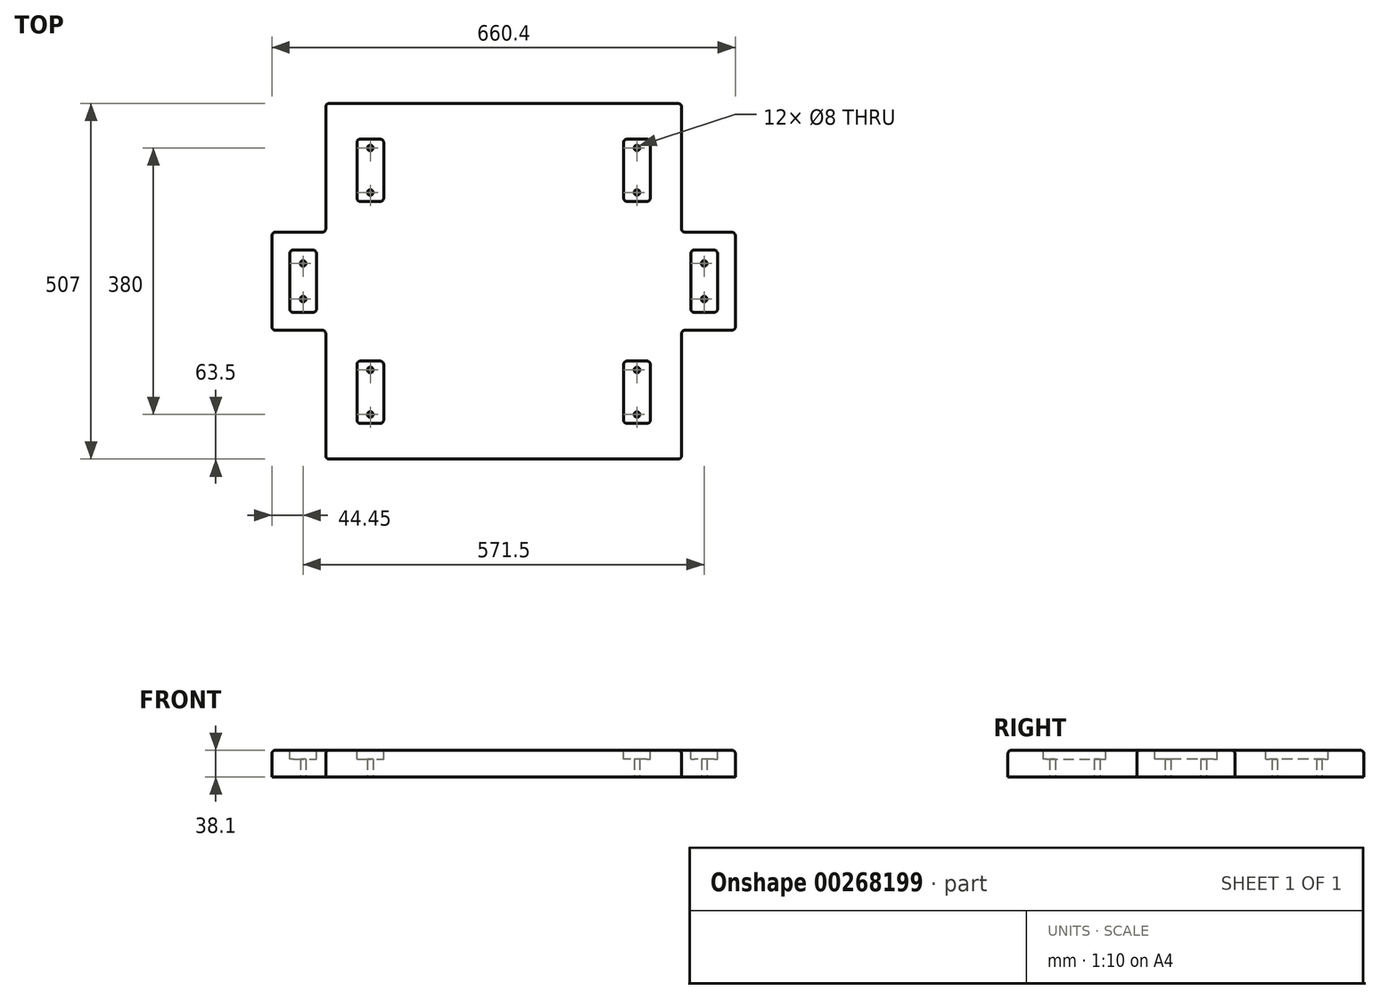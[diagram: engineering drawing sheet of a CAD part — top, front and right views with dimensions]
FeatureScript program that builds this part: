
annotation { "Feature Type Name" : "Feature", "Feature Type Description" : "" }
export const myFeature = defineFeature(function(context is Context, id is Id, definition is map)
    precondition{}
    {
        {
            var Q0;
            Q0=qCreatedBy(makeId("Top.planeOp"),FACE);
            var sketch = newSketch(context, id + "F0", { "sketchPlane" : qUnion([Q0])});
            skLineSegment(sketch, "E0.bottom", {"start": v(-253.5, 253.5) * mm, "end": v(253.5, 253.5) * mm});
            skLineSegment(sketch, "E0.top", {"start": v(-253.5, -253.5) * mm, "end": v(253.5, -253.5) * mm});
            skLineSegment(sketch, "E0.left", {"start": v(-253.5, 253.5) * mm, "end": v(-253.5, 69.85) * mm});
            skLineSegment(sketch, "E0.right", {"start": v(253.5, 253.5) * mm, "end": v(253.5, 69.85) * mm});
            skCircle(sketch, "E1", {"center": v(-190, 190) * mm, "radius": 4 * mm});
            skCircle(sketch, "E2", {"center": v(-190, 126.5) * mm, "radius": 4 * mm});
            skCircle(sketch, "E3.MirrorC", {"center": v(190, 126.5) * mm, "radius": 4 * mm});
            skCircle(sketch, "E4.MirrorC", {"center": v(190, 190) * mm, "radius": 4 * mm});
            skCircle(sketch, "E5.MirrorC", {"center": v(190, -190) * mm, "radius": 4 * mm});
            skCircle(sketch, "E6.MirrorC", {"center": v(190, -126.5) * mm, "radius": 4 * mm});
            skCircle(sketch, "E7.MirrorC", {"center": v(-190, -126.5) * mm, "radius": 4 * mm});
            skCircle(sketch, "E8.MirrorC", {"center": v(-190, -190) * mm, "radius": 4 * mm});
            skLineSegment(sketch, "E9.bottom", {"start": v(330.2, 69.85) * mm, "end": v(253.5, 69.85) * mm});
            skLineSegment(sketch, "E9.top", {"start": v(330.2, -69.85) * mm, "end": v(253.5, -69.85) * mm});
            skLineSegment(sketch, "E9.left", {"start": v(330.2, 69.85) * mm, "end": v(330.2, -69.85) * mm});
            skLineSegment(sketch, "E9.right", {"start": v(-330.2, 69.85) * mm, "end": v(-330.2, -69.85) * mm});
            skLineSegment(sketch, "E10.trimOffspring", {"start": v(-253.5, 69.85) * mm, "end": v(-330.2, 69.85) * mm});
            skLineSegment(sketch, "E11.trimOffspring", {"start": v(-253.5, -69.85) * mm, "end": v(-253.5, -253.5) * mm});
            skLineSegment(sketch, "E12.trimOffspring", {"start": v(-253.5, -69.85) * mm, "end": v(-330.2, -69.85) * mm});
            skLineSegment(sketch, "E13.trimOffspring", {"start": v(253.5, -69.85) * mm, "end": v(253.5, -253.5) * mm});
            skCircle(sketch, "E14", {"center": v(-285.75, 25.4) * mm, "radius": 4 * mm});
            skCircle(sketch, "E15.MirrorC", {"center": v(-285.75, -25.4) * mm, "radius": 4 * mm});
            skCircle(sketch, "E16.MirrorC", {"center": v(285.75, -25.4) * mm, "radius": 4 * mm});
            skCircle(sketch, "E17.MirrorC", {"center": v(285.75, 25.4) * mm, "radius": 4 * mm});
            skSolve(sketch);
        }
        {
            var Q0;
            Q0=makeQuery(id+"F0.imprint","IMPRINT",FACE,{"disambiguationData":[TD([[makeQuery(id+"F0.imprint","IMPRINT",EDGE,{"derivedFrom":sQuery(id+"F0.wireOp",EDGE,"E0.bottom")}),-1.0]])]});
            extrude(context, id + "F1", {"entities" : qUnion([Q0]), "depth" : 38.1 * mm});
        }
        {
            var Q0;
            Q0=makeQuery(id+"F1.opExtrude","CAP_EDGE",EDGE,{"disambiguationData":[OSD([sQuery(id+"F0.wireOp",EDGE,"E0.top")])],"isStart":false});
            var Q1;
            Q1=makeQuery(id+"F1.opExtrude","CAP_EDGE",EDGE,{"disambiguationData":[OSD([sQuery(id+"F0.wireOp",EDGE,"E11.trimOffspring")])],"isStart":false});
            var Q2;
            Q2=makeQuery(id+"F1.opExtrude","SWEPT_EDGE",EDGE,{"disambiguationData":[OSD([sQuery(id+"F0.wireOp",EDGE,"E0.top"),sQuery(id+"F0.wireOp",EDGE,"E11.trimOffspring")])]});
            var Q3;
            Q3=makeQuery(id+"F1.opExtrude","SWEPT_EDGE",EDGE,{"disambiguationData":[OSD([sQuery(id+"F0.wireOp",EDGE,"E11.trimOffspring"),sQuery(id+"F0.wireOp",EDGE,"E12.trimOffspring")])]});
            var Q4;
            Q4=makeQuery(id+"F1.opExtrude","CAP_EDGE",EDGE,{"disambiguationData":[OSD([sQuery(id+"F0.wireOp",EDGE,"E12.trimOffspring")])],"isStart":false});
            var Q5;
            Q5=makeQuery(id+"F1.opExtrude","SWEPT_EDGE",EDGE,{"disambiguationData":[OSD([sQuery(id+"F0.wireOp",EDGE,"E9.right"),sQuery(id+"F0.wireOp",EDGE,"E12.trimOffspring")])]});
            var Q6;
            Q6=makeQuery(id+"F1.opExtrude","CAP_EDGE",EDGE,{"disambiguationData":[OSD([sQuery(id+"F0.wireOp",EDGE,"E9.right")])],"isStart":false});
            var Q7;
            Q7=makeQuery(id+"F1.opExtrude","CAP_EDGE",EDGE,{"disambiguationData":[OSD([sQuery(id+"F0.wireOp",EDGE,"E10.trimOffspring")])],"isStart":false});
            var Q8;
            Q8=makeQuery(id+"F1.opExtrude","CAP_EDGE",EDGE,{"disambiguationData":[OSD([sQuery(id+"F0.wireOp",EDGE,"E0.left")])],"isStart":false});
            var Q9;
            Q9=makeQuery(id+"F1.opExtrude","CAP_EDGE",EDGE,{"disambiguationData":[OSD([sQuery(id+"F0.wireOp",EDGE,"E0.bottom")])],"isStart":false});
            var Q10;
            Q10=makeQuery(id+"F1.opExtrude","CAP_EDGE",EDGE,{"disambiguationData":[OSD([sQuery(id+"F0.wireOp",EDGE,"E0.right")])],"isStart":false});
            var Q11;
            Q11=makeQuery(id+"F1.opExtrude","CAP_EDGE",EDGE,{"disambiguationData":[OSD([sQuery(id+"F0.wireOp",EDGE,"E9.bottom")])],"isStart":false});
            var Q12;
            Q12=makeQuery(id+"F1.opExtrude","SWEPT_EDGE",EDGE,{"disambiguationData":[OSD([sQuery(id+"F0.wireOp",EDGE,"E0.right"),sQuery(id+"F0.wireOp",EDGE,"E9.bottom")])]});
            var Q13;
            Q13=makeQuery(id+"F1.opExtrude","SWEPT_EDGE",EDGE,{"disambiguationData":[OSD([sQuery(id+"F0.wireOp",EDGE,"E0.bottom"),sQuery(id+"F0.wireOp",EDGE,"E0.right")])]});
            var Q14;
            Q14=makeQuery(id+"F1.opExtrude","SWEPT_EDGE",EDGE,{"disambiguationData":[OSD([sQuery(id+"F0.wireOp",EDGE,"E0.bottom"),sQuery(id+"F0.wireOp",EDGE,"E0.left")])]});
            var Q15;
            Q15=makeQuery(id+"F1.opExtrude","SWEPT_EDGE",EDGE,{"disambiguationData":[OSD([sQuery(id+"F0.wireOp",EDGE,"E0.left"),sQuery(id+"F0.wireOp",EDGE,"E10.trimOffspring")])]});
            var Q16;
            Q16=makeQuery(id+"F1.opExtrude","SWEPT_EDGE",EDGE,{"disambiguationData":[OSD([sQuery(id+"F0.wireOp",EDGE,"E9.right"),sQuery(id+"F0.wireOp",EDGE,"E10.trimOffspring")])]});
            var Q17;
            Q17=makeQuery(id+"F1.opExtrude","CAP_EDGE",EDGE,{"disambiguationData":[OSD([sQuery(id+"F0.wireOp",EDGE,"E9.top")])],"isStart":false});
            var Q18;
            Q18=makeQuery(id+"F1.opExtrude","CAP_EDGE",EDGE,{"disambiguationData":[OSD([sQuery(id+"F0.wireOp",EDGE,"E9.left")])],"isStart":false});
            var Q19;
            Q19=makeQuery(id+"F1.opExtrude","SWEPT_EDGE",EDGE,{"disambiguationData":[OSD([sQuery(id+"F0.wireOp",EDGE,"E9.bottom"),sQuery(id+"F0.wireOp",EDGE,"E9.left")])]});
            var Q20;
            Q20=makeQuery(id+"F1.opExtrude","SWEPT_EDGE",EDGE,{"disambiguationData":[OSD([sQuery(id+"F0.wireOp",EDGE,"E9.top"),sQuery(id+"F0.wireOp",EDGE,"E9.left")])]});
            var Q21;
            Q21=makeQuery(id+"F1.opExtrude","SWEPT_EDGE",EDGE,{"disambiguationData":[OSD([sQuery(id+"F0.wireOp",EDGE,"E9.top"),sQuery(id+"F0.wireOp",EDGE,"E13.trimOffspring")])]});
            var Q22;
            Q22=makeQuery(id+"F1.opExtrude","CAP_EDGE",EDGE,{"disambiguationData":[OSD([sQuery(id+"F0.wireOp",EDGE,"E13.trimOffspring")])],"isStart":false});
            var Q23;
            Q23=makeQuery(id+"F1.opExtrude","SWEPT_EDGE",EDGE,{"disambiguationData":[OSD([sQuery(id+"F0.wireOp",EDGE,"E0.top"),sQuery(id+"F0.wireOp",EDGE,"E13.trimOffspring")])]});
            fillet(context, id + "F2", {"entities" : qUnion([Q0, Q1, Q2, Q3, Q4, Q5, Q6, Q7, Q8, Q9, Q10, Q11, Q12, Q13, Q14, Q15, Q16, Q17, Q18, Q19, Q20, Q21, Q22, Q23]), "radius" : 5 * mm, "tangentPropagation" : true, "allowEdgeOverflow" : false});
        }
        {
            var Q0;
            Q0=makeQuery(id+"F1.opExtrude","CAP_FACE",FACE,{"disambiguationData":[OSD([sQuery(id+"F0.wireOp",EDGE,"E0.bottom"),sQuery(id+"F0.wireOp",EDGE,"E0.top"),sQuery(id+"F0.wireOp",EDGE,"E0.left"),sQuery(id+"F0.wireOp",EDGE,"E0.right"),sQuery(id+"F0.wireOp",EDGE,"E1"),sQuery(id+"F0.wireOp",EDGE,"E2"),sQuery(id+"F0.wireOp",EDGE,"E3.MirrorC"),sQuery(id+"F0.wireOp",EDGE,"E4.MirrorC"),sQuery(id+"F0.wireOp",EDGE,"E5.MirrorC"),sQuery(id+"F0.wireOp",EDGE,"E6.MirrorC"),sQuery(id+"F0.wireOp",EDGE,"E7.MirrorC"),sQuery(id+"F0.wireOp",EDGE,"E8.MirrorC"),sQuery(id+"F0.wireOp",EDGE,"E9.bottom"),sQuery(id+"F0.wireOp",EDGE,"E9.top"),sQuery(id+"F0.wireOp",EDGE,"E9.left"),sQuery(id+"F0.wireOp",EDGE,"E9.right"),sQuery(id+"F0.wireOp",EDGE,"E10.trimOffspring"),sQuery(id+"F0.wireOp",EDGE,"E11.trimOffspring"),sQuery(id+"F0.wireOp",EDGE,"E12.trimOffspring"),sQuery(id+"F0.wireOp",EDGE,"E13.trimOffspring"),sQuery(id+"F0.wireOp",EDGE,"E14"),sQuery(id+"F0.wireOp",EDGE,"E15.MirrorC"),sQuery(id+"F0.wireOp",EDGE,"E16.MirrorC"),sQuery(id+"F0.wireOp",EDGE,"E17.MirrorC")])],"isStart":false});
            var sketch = newSketch(context, id + "F3", { "sketchPlane" : qUnion([Q0])});
            skLineSegment(sketch, "E18.bottom", {"start": v(-304.8, 44.45) * mm, "end": v(-266.7, 44.45) * mm});
            skLineSegment(sketch, "E18.top", {"start": v(-304.8, -44.45) * mm, "end": v(-266.7, -44.45) * mm});
            skLineSegment(sketch, "E18.left", {"start": v(-304.8, 44.45) * mm, "end": v(-304.8, -44.45) * mm});
            skLineSegment(sketch, "E18.right", {"start": v(-266.7, 44.45) * mm, "end": v(-266.7, -44.45) * mm});
            skLineSegment(sketch, "E19.MirrorCS", {"start": v(304.8, 44.45) * mm, "end": v(266.7, 44.45) * mm});
            skLineSegment(sketch, "E20.MirrorCS", {"start": v(266.7, 44.45) * mm, "end": v(266.7, -44.45) * mm});
            skLineSegment(sketch, "E21.MirrorCS", {"start": v(304.8, 44.45) * mm, "end": v(304.8, -44.45) * mm});
            skLineSegment(sketch, "E22.MirrorCS", {"start": v(304.8, -44.45) * mm, "end": v(266.7, -44.45) * mm});
            skLineSegment(sketch, "E23.bottom", {"start": v(-209.05, 202.7) * mm, "end": v(-170.95, 202.7) * mm});
            skLineSegment(sketch, "E23.top", {"start": v(-209.05, 113.8) * mm, "end": v(-170.95, 113.8) * mm});
            skLineSegment(sketch, "E23.left", {"start": v(-209.05, 202.7) * mm, "end": v(-209.05, 113.8) * mm});
            skLineSegment(sketch, "E23.right", {"start": v(-170.95, 202.7) * mm, "end": v(-170.95, 113.8) * mm});
            skLineSegment(sketch, "E24.MirrorCS", {"start": v(209.05, 202.7) * mm, "end": v(170.95, 202.7) * mm});
            skLineSegment(sketch, "E25.MirrorCS", {"start": v(209.05, 113.8) * mm, "end": v(170.95, 113.8) * mm});
            skLineSegment(sketch, "E26.MirrorCS", {"start": v(209.05, 202.7) * mm, "end": v(209.05, 113.8) * mm});
            skLineSegment(sketch, "E27.MirrorCS", {"start": v(170.95, 202.7) * mm, "end": v(170.95, 113.8) * mm});
            skLineSegment(sketch, "E28.MirrorCS", {"start": v(209.05, -113.8) * mm, "end": v(170.95, -113.8) * mm});
            skLineSegment(sketch, "E29.MirrorCS", {"start": v(209.05, -202.7) * mm, "end": v(209.05, -113.8) * mm});
            skLineSegment(sketch, "E30.MirrorCS", {"start": v(209.05, -202.7) * mm, "end": v(170.95, -202.7) * mm});
            skLineSegment(sketch, "E31.MirrorCS", {"start": v(170.95, -202.7) * mm, "end": v(170.95, -113.8) * mm});
            skLineSegment(sketch, "E32.MirrorCS", {"start": v(-209.05, -113.8) * mm, "end": v(-170.95, -113.8) * mm});
            skLineSegment(sketch, "E33.MirrorCS", {"start": v(-170.95, -202.7) * mm, "end": v(-170.95, -113.8) * mm});
            skLineSegment(sketch, "E34.MirrorCS", {"start": v(-209.05, -202.7) * mm, "end": v(-209.05, -113.8) * mm});
            skLineSegment(sketch, "E35.MirrorCS", {"start": v(-209.05, -202.7) * mm, "end": v(-170.95, -202.7) * mm});
            skSolve(sketch);
        }
        {
            var Q0;
            Q0=makeQuery(id+"F3.imprint","IMPRINT",FACE,{"disambiguationData":[TD([[makeQuery(id+"F3.imprint","IMPRINT",EDGE,{"derivedFrom":sQuery(id+"F3.wireOp",EDGE,"E23.bottom")}),-1.0]])]});
            var Q1;
            Q1=makeQuery(id+"F3.imprint","IMPRINT",FACE,{"disambiguationData":[TD([[makeQuery(id+"F3.imprint","IMPRINT",EDGE,{"derivedFrom":sQuery(id+"F3.wireOp",EDGE,"E24.MirrorCS")}),1.0]])]});
            var Q2;
            Q2=makeQuery(id+"F3.imprint","IMPRINT",FACE,{"disambiguationData":[TD([[makeQuery(id+"F3.imprint","IMPRINT",EDGE,{"derivedFrom":sQuery(id+"F3.wireOp",EDGE,"E19.MirrorCS")}),1.0]])]});
            var Q3;
            Q3=makeQuery(id+"F3.imprint","IMPRINT",FACE,{"disambiguationData":[TD([[makeQuery(id+"F3.imprint","IMPRINT",EDGE,{"derivedFrom":sQuery(id+"F3.wireOp",EDGE,"E28.MirrorCS")}),1.0]])]});
            var Q4;
            Q4=makeQuery(id+"F3.imprint","IMPRINT",FACE,{"disambiguationData":[TD([[makeQuery(id+"F3.imprint","IMPRINT",EDGE,{"derivedFrom":sQuery(id+"F3.wireOp",EDGE,"E32.MirrorCS")}),-1.0]])]});
            var Q5;
            Q5=makeQuery(id+"F3.imprint","IMPRINT",FACE,{"disambiguationData":[TD([[makeQuery(id+"F3.imprint","IMPRINT",EDGE,{"derivedFrom":sQuery(id+"F3.wireOp",EDGE,"E18.bottom")}),-1.0]])]});
            extrude(context, id + "F4", {"entities" : qUnion([Q0, Q1, Q2, Q3, Q4, Q5]), "operationType" : NewBodyOperationType.REMOVE, "oppositeDirection" : true, "depth" : 12.75 * mm});
        }
        {
            var Q0;
            Q0=makeQuery(id+"F4.boolean.opBoolean","COPY",EDGE,{"derivedFrom":makeQuery(id+"F4.opExtrude","SWEPT_EDGE",EDGE,{"disambiguationData":[OSD([sQuery(id+"F3.wireOp",EDGE,"E24.MirrorCS"),sQuery(id+"F3.wireOp",EDGE,"E27.MirrorCS")])]})});
            var Q1;
            Q1=makeQuery(id+"F4.boolean.opBoolean","COPY",EDGE,{"derivedFrom":makeQuery(id+"F4.opExtrude","SWEPT_EDGE",EDGE,{"disambiguationData":[OSD([sQuery(id+"F3.wireOp",EDGE,"E25.MirrorCS"),sQuery(id+"F3.wireOp",EDGE,"E27.MirrorCS")])]})});
            var Q2;
            Q2=makeQuery(id+"F4.boolean.opBoolean","COPY",EDGE,{"derivedFrom":makeQuery(id+"F4.opExtrude","SWEPT_EDGE",EDGE,{"disambiguationData":[OSD([sQuery(id+"F3.wireOp",EDGE,"E24.MirrorCS"),sQuery(id+"F3.wireOp",EDGE,"E26.MirrorCS")])]})});
            var Q3;
            Q3=makeQuery(id+"F4.boolean.opBoolean","COPY",EDGE,{"derivedFrom":makeQuery(id+"F4.opExtrude","SWEPT_EDGE",EDGE,{"disambiguationData":[OSD([sQuery(id+"F3.wireOp",EDGE,"E25.MirrorCS"),sQuery(id+"F3.wireOp",EDGE,"E26.MirrorCS")])]})});
            var Q4;
            Q4=makeQuery(id+"F4.boolean.opBoolean","COPY",EDGE,{"derivedFrom":makeQuery(id+"F4.opExtrude","SWEPT_EDGE",EDGE,{"disambiguationData":[OSD([sQuery(id+"F3.wireOp",EDGE,"E21.MirrorCS"),sQuery(id+"F3.wireOp",EDGE,"E22.MirrorCS")])]})});
            var Q5;
            Q5=makeQuery(id+"F4.boolean.opBoolean","COPY",EDGE,{"derivedFrom":makeQuery(id+"F4.opExtrude","SWEPT_EDGE",EDGE,{"disambiguationData":[OSD([sQuery(id+"F3.wireOp",EDGE,"E19.MirrorCS"),sQuery(id+"F3.wireOp",EDGE,"E21.MirrorCS")])]})});
            var Q6;
            Q6=makeQuery(id+"F4.boolean.opBoolean","COPY",EDGE,{"derivedFrom":makeQuery(id+"F4.opExtrude","SWEPT_EDGE",EDGE,{"disambiguationData":[OSD([sQuery(id+"F3.wireOp",EDGE,"E19.MirrorCS"),sQuery(id+"F3.wireOp",EDGE,"E20.MirrorCS")])]})});
            var Q7;
            Q7=makeQuery(id+"F4.boolean.opBoolean","COPY",EDGE,{"derivedFrom":makeQuery(id+"F4.opExtrude","SWEPT_EDGE",EDGE,{"disambiguationData":[OSD([sQuery(id+"F3.wireOp",EDGE,"E20.MirrorCS"),sQuery(id+"F3.wireOp",EDGE,"E22.MirrorCS")])]})});
            var Q8;
            Q8=makeQuery(id+"F4.boolean.opBoolean","COPY",EDGE,{"derivedFrom":makeQuery(id+"F4.opExtrude","SWEPT_EDGE",EDGE,{"disambiguationData":[OSD([sQuery(id+"F3.wireOp",EDGE,"E30.MirrorCS"),sQuery(id+"F3.wireOp",EDGE,"E31.MirrorCS")])]})});
            var Q9;
            Q9=makeQuery(id+"F4.boolean.opBoolean","COPY",EDGE,{"derivedFrom":makeQuery(id+"F4.opExtrude","SWEPT_EDGE",EDGE,{"disambiguationData":[OSD([sQuery(id+"F3.wireOp",EDGE,"E28.MirrorCS"),sQuery(id+"F3.wireOp",EDGE,"E31.MirrorCS")])]})});
            var Q10;
            Q10=makeQuery(id+"F4.boolean.opBoolean","COPY",EDGE,{"derivedFrom":makeQuery(id+"F4.opExtrude","SWEPT_EDGE",EDGE,{"disambiguationData":[OSD([sQuery(id+"F3.wireOp",EDGE,"E28.MirrorCS"),sQuery(id+"F3.wireOp",EDGE,"E29.MirrorCS")])]})});
            var Q11;
            Q11=makeQuery(id+"F4.boolean.opBoolean","COPY",EDGE,{"derivedFrom":makeQuery(id+"F4.opExtrude","SWEPT_EDGE",EDGE,{"disambiguationData":[OSD([sQuery(id+"F3.wireOp",EDGE,"E29.MirrorCS"),sQuery(id+"F3.wireOp",EDGE,"E30.MirrorCS")])]})});
            var Q12;
            Q12=makeQuery(id+"F4.boolean.opBoolean","COPY",EDGE,{"derivedFrom":makeQuery(id+"F4.opExtrude","SWEPT_EDGE",EDGE,{"disambiguationData":[OSD([sQuery(id+"F3.wireOp",EDGE,"E32.MirrorCS"),sQuery(id+"F3.wireOp",EDGE,"E34.MirrorCS")])]})});
            var Q13;
            Q13=makeQuery(id+"F4.boolean.opBoolean","COPY",EDGE,{"derivedFrom":makeQuery(id+"F4.opExtrude","SWEPT_EDGE",EDGE,{"disambiguationData":[OSD([sQuery(id+"F3.wireOp",EDGE,"E32.MirrorCS"),sQuery(id+"F3.wireOp",EDGE,"E33.MirrorCS")])]})});
            var Q14;
            Q14=makeQuery(id+"F4.boolean.opBoolean","COPY",EDGE,{"derivedFrom":makeQuery(id+"F4.opExtrude","SWEPT_EDGE",EDGE,{"disambiguationData":[OSD([sQuery(id+"F3.wireOp",EDGE,"E33.MirrorCS"),sQuery(id+"F3.wireOp",EDGE,"E35.MirrorCS")])]})});
            var Q15;
            Q15=makeQuery(id+"F4.boolean.opBoolean","COPY",EDGE,{"derivedFrom":makeQuery(id+"F4.opExtrude","SWEPT_EDGE",EDGE,{"disambiguationData":[OSD([sQuery(id+"F3.wireOp",EDGE,"E34.MirrorCS"),sQuery(id+"F3.wireOp",EDGE,"E35.MirrorCS")])]})});
            var Q16;
            Q16=makeQuery(id+"F4.boolean.opBoolean","COPY",EDGE,{"derivedFrom":makeQuery(id+"F4.opExtrude","SWEPT_EDGE",EDGE,{"disambiguationData":[OSD([sQuery(id+"F3.wireOp",EDGE,"E18.top"),sQuery(id+"F3.wireOp",EDGE,"E18.left")])]})});
            var Q17;
            Q17=makeQuery(id+"F4.boolean.opBoolean","COPY",EDGE,{"derivedFrom":makeQuery(id+"F4.opExtrude","SWEPT_EDGE",EDGE,{"disambiguationData":[OSD([sQuery(id+"F3.wireOp",EDGE,"E18.top"),sQuery(id+"F3.wireOp",EDGE,"E18.right")])]})});
            var Q18;
            Q18=makeQuery(id+"F4.boolean.opBoolean","COPY",EDGE,{"derivedFrom":makeQuery(id+"F4.opExtrude","SWEPT_EDGE",EDGE,{"disambiguationData":[OSD([sQuery(id+"F3.wireOp",EDGE,"E18.bottom"),sQuery(id+"F3.wireOp",EDGE,"E18.right")])]})});
            var Q19;
            Q19=makeQuery(id+"F4.boolean.opBoolean","COPY",EDGE,{"derivedFrom":makeQuery(id+"F4.opExtrude","SWEPT_EDGE",EDGE,{"disambiguationData":[OSD([sQuery(id+"F3.wireOp",EDGE,"E18.bottom"),sQuery(id+"F3.wireOp",EDGE,"E18.left")])]})});
            var Q20;
            Q20=makeQuery(id+"F4.boolean.opBoolean","COPY",EDGE,{"derivedFrom":makeQuery(id+"F4.opExtrude","SWEPT_EDGE",EDGE,{"disambiguationData":[OSD([sQuery(id+"F3.wireOp",EDGE,"E23.bottom"),sQuery(id+"F3.wireOp",EDGE,"E23.left")])]})});
            var Q21;
            Q21=makeQuery(id+"F4.boolean.opBoolean","COPY",EDGE,{"derivedFrom":makeQuery(id+"F4.opExtrude","SWEPT_EDGE",EDGE,{"disambiguationData":[OSD([sQuery(id+"F3.wireOp",EDGE,"E23.bottom"),sQuery(id+"F3.wireOp",EDGE,"E23.right")])]})});
            var Q22;
            Q22=makeQuery(id+"F4.boolean.opBoolean","COPY",EDGE,{"derivedFrom":makeQuery(id+"F4.opExtrude","SWEPT_EDGE",EDGE,{"disambiguationData":[OSD([sQuery(id+"F3.wireOp",EDGE,"E23.top"),sQuery(id+"F3.wireOp",EDGE,"E23.right")])]})});
            var Q23;
            Q23=makeQuery(id+"F4.boolean.opBoolean","COPY",EDGE,{"derivedFrom":makeQuery(id+"F4.opExtrude","SWEPT_EDGE",EDGE,{"disambiguationData":[OSD([sQuery(id+"F3.wireOp",EDGE,"E23.top"),sQuery(id+"F3.wireOp",EDGE,"E23.left")])]})});
            fillet(context, id + "F5", {"entities" : qUnion([Q0, Q1, Q2, Q3, Q4, Q5, Q6, Q7, Q8, Q9, Q10, Q11, Q12, Q13, Q14, Q15, Q16, Q17, Q18, Q19, Q20, Q21, Q22, Q23]), "radius" : 5 * mm, "tangentPropagation" : true, "allowEdgeOverflow" : false});
        }
    });
